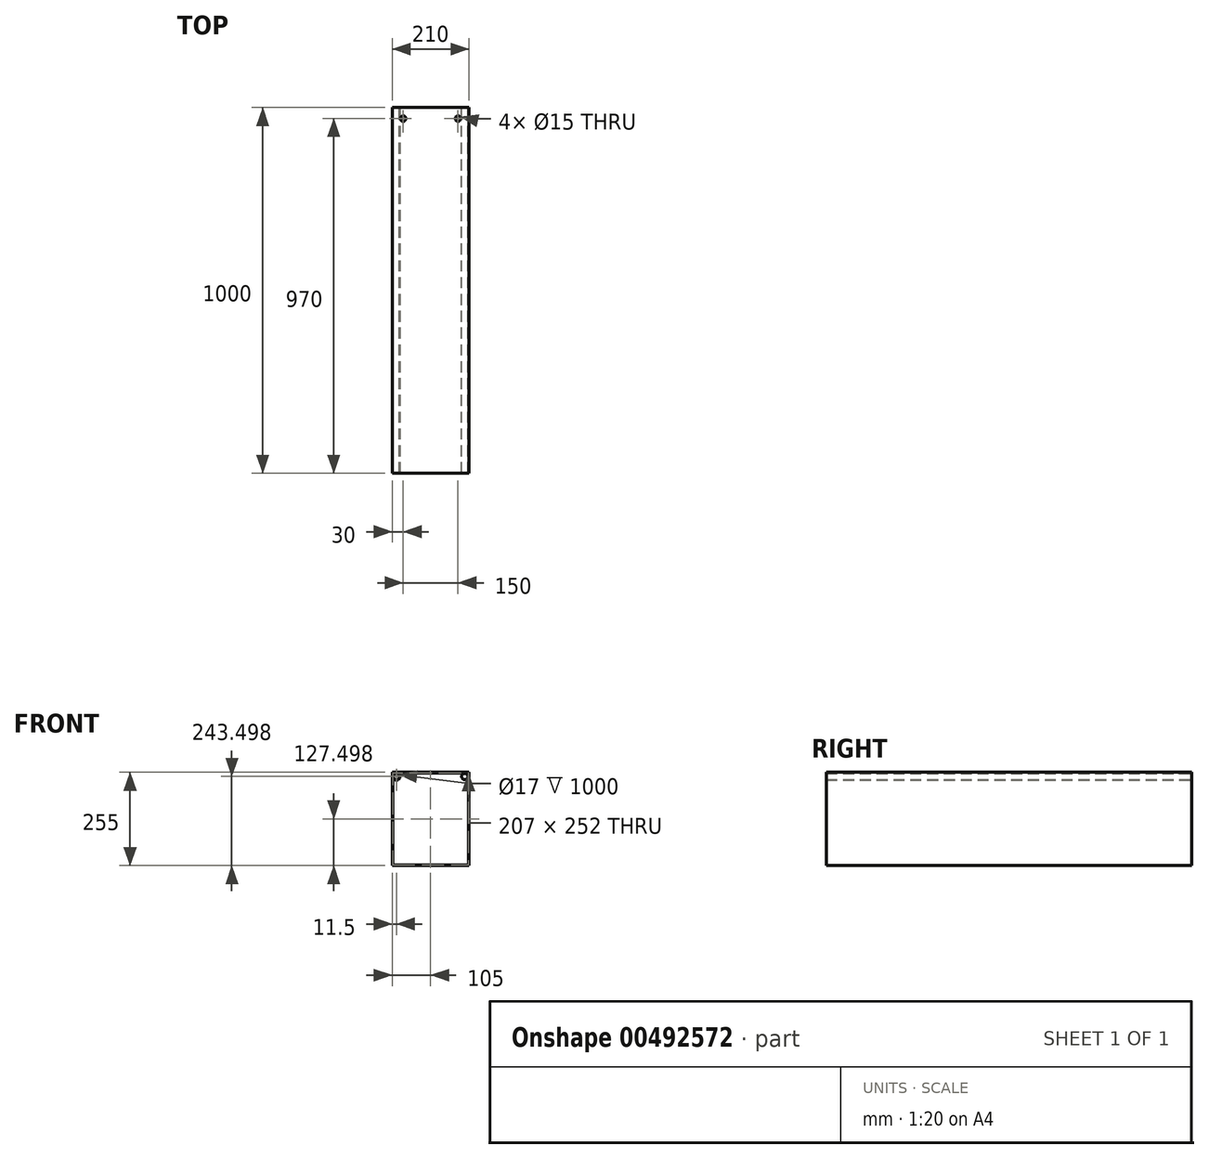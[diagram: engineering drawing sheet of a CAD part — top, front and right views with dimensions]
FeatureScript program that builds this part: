
annotation { "Feature Type Name" : "Feature", "Feature Type Description" : "" }
export const myFeature = defineFeature(function(context is Context, id is Id, definition is map)
    precondition{}
    {
        {
            var Q0;
            Q0=qCreatedBy(makeId("Front.planeOp"),FACE);
            var sketch = newSketch(context, id + "F0", { "sketchPlane" : qUnion([Q0])});
            skLineSegment(sketch, "E0.bottom", {"start": v(-105, -138.46) * mm, "end": v(105, -138.46) * mm});
            skLineSegment(sketch, "E0.top", {"start": v(-105, 116.54) * mm, "end": v(105, 116.54) * mm});
            skLineSegment(sketch, "E0.left", {"start": v(-105, -138.46) * mm, "end": v(-105, 116.54) * mm});
            skLineSegment(sketch, "E0.right", {"start": v(105, -138.46) * mm, "end": v(105, 116.54) * mm});
            skLineSegment(sketch, "E1.0", {"start": v(-103.5, 115.04) * mm, "end": v(103.5, 115.04) * mm});
            skLineSegment(sketch, "E1.1", {"start": v(-103.5, -136.96) * mm, "end": v(-103.5, 115.04) * mm});
            skLineSegment(sketch, "E1.2", {"start": v(-103.5, -136.96) * mm, "end": v(103.5, -136.96) * mm});
            skLineSegment(sketch, "E1.3", {"start": v(103.5, -136.96) * mm, "end": v(103.5, 115.04) * mm});
            skCircle(sketch, "E2", {"center": v(-93.5, 105.04) * mm, "radius": 10 * mm});
            skCircle(sketch, "E3.0", {"center": v(-93.5, 105.04) * mm, "radius": 8.5 * mm});
            skLineSegment(sketch, "E4", {"start": v(0, 115.04) * mm, "end": v(0, 60.06) * mm, "construction": true});
            skCircle(sketch, "E5.MirrorC", {"center": v(93.5, 105.04) * mm, "radius": 8.5 * mm});
            skCircle(sketch, "E6.MirrorC", {"center": v(93.5, 105.04) * mm, "radius": 10 * mm});
            skSolve(sketch);
        }
        {
            var Q0;
            Q0=makeQuery(id+"F0.imprint","IMPRINT",FACE,{"disambiguationData":[TD([[makeQuery(id+"F0.imprint","IMPRINT",EDGE,{"derivedFrom":sQuery(id+"F0.wireOp",EDGE,"E3.0")}),-1.0]])]});
            var Q1;
            Q1=makeQuery(id+"F0.imprint","IMPRINT",FACE,{"disambiguationData":[TD([[makeQuery(id+"F0.imprint","IMPRINT",EDGE,{"derivedFrom":sQuery(id+"F0.wireOp",EDGE,"E0.bottom")}),1.0]])]});
            var Q2;
            Q2=makeQuery(id+"F0.imprint","IMPRINT",FACE,{"disambiguationData":[TD([[makeQuery(id+"F0.imprint","IMPRINT",EDGE,{"derivedFrom":sQuery(id+"F0.wireOp",EDGE,"E5.MirrorC")}),1.0]])]});
            extrude(context, id + "F1", {"entities" : qUnion([Q0, Q1, Q2]), "depth" : 1000 * mm, "offsetDistance" : 25 * mm});
        }
        {
            var Q0;
            Q0=makeQuery(id+"F1.opExtrude","SWEPT_FACE",FACE,{"disambiguationData":[OSD([sQuery(id+"F0.wireOp",EDGE,"E0.top")])]});
            var sketch = newSketch(context, id + "F2", { "sketchPlane" : qUnion([Q0])});
            skLineSegment(sketch, "E7", {"start": v(-106.79, -30) * mm, "end": v(101.88, -30) * mm, "construction": true});
            skPoint(sketch, "E8", {"position": v(-75, -30) * mm});
            skPoint(sketch, "E9", {"position": v(75, -30) * mm});
            skLineSegment(sketch, "E10", {"start": v(0, 0) * mm, "end": v(0, -86.04) * mm, "construction": true});
            skSolve(sketch);
        }
        {
            var Q0;
            Q0=sQuery(id+"F2.wireOp",VERTEX,"E9");
            var Q1;
            Q1=sQuery(id+"F2.wireOp",VERTEX,"E8");
            var Q2;
            Q2=makeQuery(id+"F1.opExtrude","SWEPT_BODY",BODY,{"disambiguationData":[OSD([sQuery(id+"F0.wireOp",EDGE,"E0.bottom"),sQuery(id+"F0.wireOp",EDGE,"E0.top"),sQuery(id+"F0.wireOp",EDGE,"E0.left"),sQuery(id+"F0.wireOp",EDGE,"E0.right"),sQuery(id+"F0.wireOp",EDGE,"E1.0"),sQuery(id+"F0.wireOp",EDGE,"E1.1"),sQuery(id+"F0.wireOp",EDGE,"E1.2"),sQuery(id+"F0.wireOp",EDGE,"E1.3")])]});
            hole(context, id + "F3", {"style" : HoleStyle.SIMPLE, "endStyle" : HoleEndStyle.THROUGH, "standardTappedOrClearance" : lookupTablePath({ "standard" : "ISO", "size" : "15", "type" : "Drilled" }), "standardBlindInLast" : lookupTablePath({ "standard" : "ISO", "size" : "15", "type" : "Drilled" }), "holeDiameter" : 15 * mm, "majorDiameter" : 5 * mm, "isTappedThrough" : true, "tappedDepth" : 12 * mm, "tapClearance" : 3, "startFromSketch" : true, "locations" : qUnion([Q0, Q1]), "scope" : qUnion([Q2])});
        }
    });
